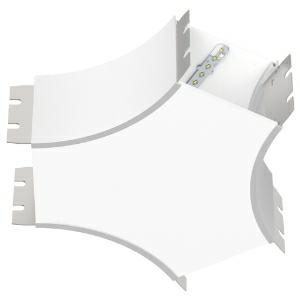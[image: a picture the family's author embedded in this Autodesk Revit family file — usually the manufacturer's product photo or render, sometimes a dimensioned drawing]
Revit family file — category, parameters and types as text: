
# Revit family: super-g_super-g_kreuzung_hl_led__8_4w_1100lm_3000k_cri_80_430-1440_78b1
name_source: partatom
category: Leuchten
revit_build: Autodesk Revit 2016 (Build: 20190508_0715(x64)
units: mm (PartAtom-declared; Revit-internal decimal feet)

## family parameters
Basisbauteil = Fläche
Beim Laden mit Abzugskörper schneiden = Nein
Bemaßung runder Anschluss = Durchmesser verwenden
Gemeinsam genutzt = Nein
Lichtquelle = Nein
Raumberechnungspunkt = Nein
Teiletyp = Normal

## types (1)
- 430-1440- (3 x LED, 480 lm, 3.3 W, 3000K)
    Approval mark = CE
    Beschreibung = The insert consists of aluminum-extruded profile. Charming SOFT-EDGE design ensure unparalleled styling. The ballast is integrated and allows for an operation with 220-240V (50/60Hz). SUPER-G (# 430-1440) ist not dimmable (on/off).
    CIE Flux Codes = 44 75 94 100 65
    Color Rendering = 1B/80…89
    Color Temperature = 3000K
    Height = 120 mm
    Hersteller = Prolicht
    Lamp Light Flux = 480 lm
    Lamp Power = 3.3 W
    Lamp count = 3
    Lampe = 3 x LED
    Length = 350 mm
    Luminous efficacy = 95 lm/W
    ModVariant = Nein
    Modell = 430-1440
    Mounting Place = Ceiling
    Mounting Type = Pendant
    Number of Poles = 1
    OnlyDefault = Ja
    Power Factor = 1
    Product Name = SUPER-G__SUPER-G KREUZUNG HL LED: 8,4W 1100lm 3000K CRI:80
    Product group = Suspended profile systems
    ProductGroupID = 944
    Protection Class = Protection class I
    Protection Degree = IP 20
    RLX_Detail_Level = 1
    RlxData = <blob elided: 42349 chars, md5=3d11ca80>
    Scheinlast = 10 VA
    Socket = socket
    Standby Power = 0 W
    System Light Flux = 936 lm
    System Power = 10 W
    Typenbild = 430-1440.jpg
    URL = http://relux.com
    VarID = 430-1440-
    Voltage = 0 V
    Vorgabe-Ansicht = 1800 mm
    Weight = 0.00 kg
    Width = 303 mm

## geometry (parser evidence)
native form markers: Sweep x12
no freeform markers — native parametric forms only
